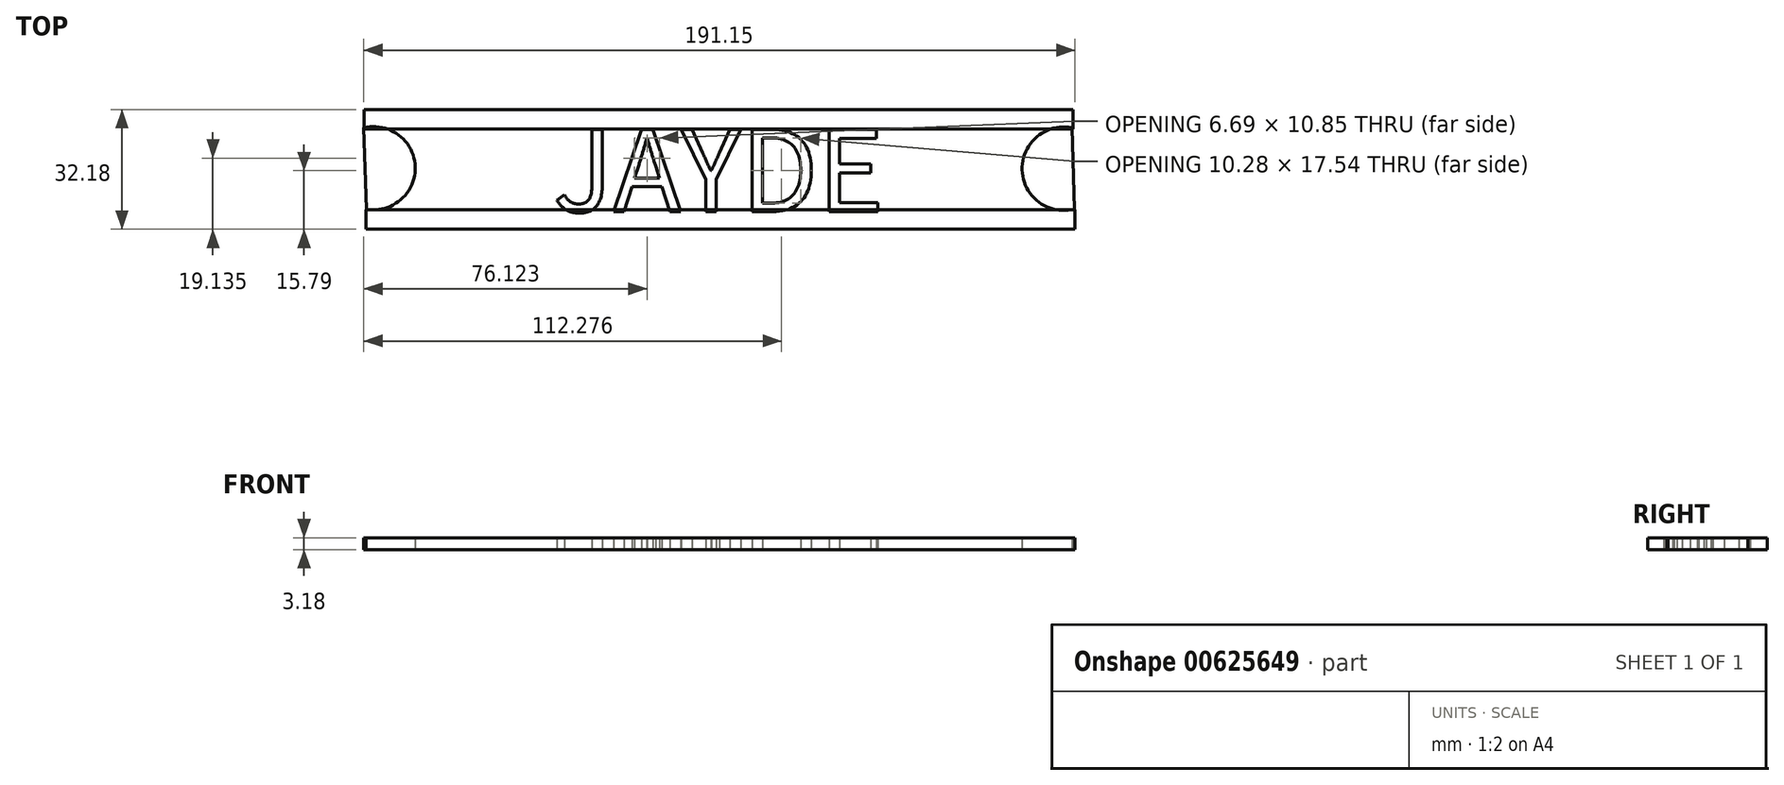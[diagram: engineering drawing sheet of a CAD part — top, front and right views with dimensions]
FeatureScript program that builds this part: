
annotation { "Feature Type Name" : "Feature", "Feature Type Description" : "" }
export const myFeature = defineFeature(function(context is Context, id is Id, definition is map)
    precondition{}
    {
        {
            var Q0;
            Q0=qCreatedBy(makeId("Top.planeOp"),FACE);
            var sketch = newSketch(context, id + "F0", { "sketchPlane" : qUnion([Q0])});
            skLineSegment(sketch, "E0.bottom", {"start": v(-94.38, 15.84) * mm, "end": v(96.12, 15.84) * mm});
            skLineSegment(sketch, "E0.top", {"start": v(-94.38, -15.91) * mm, "end": v(96.12, -15.91) * mm});
            skLineSegment(sketch, "E0.left", {"start": v(-94.38, 15.84) * mm, "end": v(-94.38, -15.91) * mm});
            skLineSegment(sketch, "E0.right", {"start": v(96.12, 15.84) * mm, "end": v(96.12, -15.91) * mm});
            skSolve(sketch);
        }
        {
            var Q0;
            Q0=makeQuery(id+"F0.imprint","IMPRINT",FACE,{"disambiguationData":[TD([[makeQuery(id+"F0.imprint","IMPRINT",EDGE,{"derivedFrom":sQuery(id+"F0.wireOp",EDGE,"E0.bottom")}),-1.0]])]});
            var sketch = newSketch(context, id + "F1", { "sketchPlane" : qUnion([Q0])});
            skLineSegment(sketch, "E1.bottom", {"start": v(-94.54, 16.38) * mm, "end": v(95.96, 16.38) * mm});
            skLineSegment(sketch, "E1.top", {"start": v(-94.54, 11.16) * mm, "end": v(95.96, 11.16) * mm});
            skLineSegment(sketch, "E1.left", {"start": v(-94.54, 16.38) * mm, "end": v(-94.54, 11.16) * mm});
            skLineSegment(sketch, "E1.right", {"start": v(95.96, 16.38) * mm, "end": v(95.96, 11.16) * mm});
            skLineSegment(sketch, "E2.bottom", {"start": v(-93.96, -15.8) * mm, "end": v(96.54, -15.8) * mm});
            skLineSegment(sketch, "E2.top", {"start": v(-93.96, -10.6) * mm, "end": v(96.54, -10.6) * mm});
            skLineSegment(sketch, "E2.left", {"start": v(-93.96, -15.8) * mm, "end": v(-93.96, -10.6) * mm});
            skLineSegment(sketch, "E2.right", {"start": v(96.54, -15.8) * mm, "end": v(96.54, -10.6) * mm});
            skSolve(sketch);
        }
        {
            var Q0;
            Q0 = qSketchRegion(id + "F1", true);
            extrude(context, id + "F2", {"entities" : qUnion([Q0]), "depth" : 3.17 * mm, "offsetDistance" : 25.4 * mm});
        }
        {
            var Q0;
            Q0=makeQuery(id+"F0.imprint","IMPRINT",FACE,{"disambiguationData":[TD([[makeQuery(id+"F0.imprint","IMPRINT",EDGE,{"derivedFrom":sQuery(id+"F0.wireOp",EDGE,"E0.bottom")}),-1.0]])]});
            var sketch = newSketch(context, id + "F3", { "sketchPlane" : qUnion([Q0])});
            skText(sketch, "E3", { "text": "JAYDE", "fontName": "NotoSansCJKjp-Regular.otf"});
            const initialGuessF3  = {"E3": [-0.04374, -0.01107, 1, 0, 0.0217]};
            skSetInitialGuess(sketch, initialGuessF3);
            skSolve(sketch);
        }
        {
            var Q0;
            Q0 = qSketchRegion(id + "F3", true);
            extrude(context, id + "F4", {"entities" : qUnion([Q0]), "depth" : 3.17 * mm, "offsetDistance" : 25.4 * mm});
        }
        {
            var Q0;
            Q0=makeQuery(id+"F0.imprint","IMPRINT",FACE,{"disambiguationData":[TD([[makeQuery(id+"F0.imprint","IMPRINT",EDGE,{"derivedFrom":sQuery(id+"F0.wireOp",EDGE,"E0.bottom")}),-1.0]])]});
            var sketch = newSketch(context, id + "F5", { "sketchPlane" : qUnion([Q0])});
            skArc(sketch, "E4", {"start": v(95.72, 11.51) * mm, "mid": v(82.33, 0.14) * mm, "end": v(96.4, -10.37) * mm});
            skArc(sketch, "E5", {"start": v(-93.93, -10.38) * mm, "mid": v(-80.76, 0.98) * mm, "end": v(-94.6, 11.5) * mm});
            skLineSegment(sketch, "E6", {"start": v(-94.6, 11.5) * mm, "end": v(-93.93, -10.38) * mm});
            skLineSegment(sketch, "E7", {"start": v(95.72, 11.51) * mm, "end": v(96.4, -10.37) * mm});
            skSolve(sketch);
        }
        {
            var Q0;
            Q0 = qSketchRegion(id + "F5", true);
            extrude(context, id + "F6", {"entities" : qUnion([Q0]), "depth" : 3.17 * mm, "offsetDistance" : 25.4 * mm});
        }
    });
